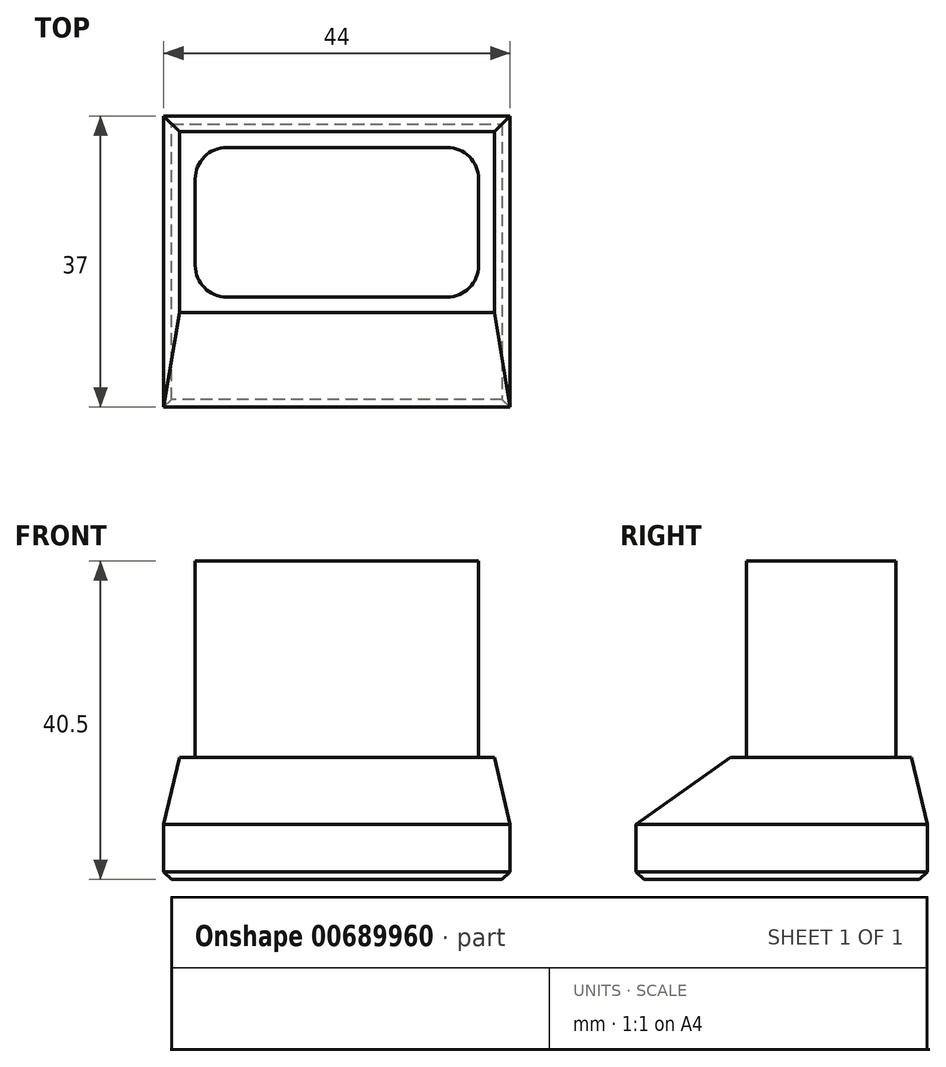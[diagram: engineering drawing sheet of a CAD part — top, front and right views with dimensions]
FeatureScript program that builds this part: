
annotation { "Feature Type Name" : "Feature", "Feature Type Description" : "" }
export const myFeature = defineFeature(function(context is Context, id is Id, definition is map)
    precondition{}
    {
        {
            var Q0;
            Q0=qCreatedBy(makeId("Top.planeOp"),FACE);
            var sketch = newSketch(context, id + "F0", { "sketchPlane" : qUnion([Q0])});
            skLineSegment(sketch, "E0.bottom", {"start": v(22, -18.5) * mm, "end": v(-22, -18.5) * mm});
            skLineSegment(sketch, "E0.top", {"start": v(22, 18.5) * mm, "end": v(-22, 18.5) * mm});
            skLineSegment(sketch, "E0.left", {"start": v(22, -18.5) * mm, "end": v(22, 18.5) * mm});
            skLineSegment(sketch, "E0.right", {"start": v(-22, -18.5) * mm, "end": v(-22, 18.5) * mm});
            skPoint(sketch, "E0.middle", {"position": v(0, 0) * mm});
            skSolve(sketch);
        }
        {
            var Q0;
            Q0=makeQuery(id+"F0.imprint","IMPRINT",FACE,{"disambiguationData":[TD([[makeQuery(id+"F0.imprint","IMPRINT",EDGE,{"derivedFrom":sQuery(id+"F0.wireOp",EDGE,"E0.bottom")}),-1.0]])]});
            extrude(context, id + "F1", {"entities" : qUnion([Q0]), "depth" : 15.5 * mm, "offsetDistance" : 25 * mm});
        }
        {
            var Q0;
            Q0=makeQuery(id+"F1.opExtrude","CAP_EDGE",EDGE,{"disambiguationData":[OSD([sQuery(id+"F0.wireOp",EDGE,"E0.bottom")])],"isStart":false});
            chamfer(context, id + "F2", {"entities" : qUnion([Q0]), "chamferType" : ChamferType.TWO_OFFSETS, "width1" : 8.5 * mm, "oppositeDirection" : false, "width2" : 12 * mm, "tangentPropagation" : true});
        }
        {
            var Q0;
            Q0=makeQuery(id+"F1.opExtrude","CAP_EDGE",EDGE,{"disambiguationData":[OSD([sQuery(id+"F0.wireOp",EDGE,"E0.right")])],"isStart":false});
            var Q1;
            Q1=makeQuery(id+"F1.opExtrude","CAP_EDGE",EDGE,{"disambiguationData":[OSD([sQuery(id+"F0.wireOp",EDGE,"E0.left")])],"isStart":false});
            var Q2;
            Q2=makeQuery(id+"F1.opExtrude","CAP_EDGE",EDGE,{"disambiguationData":[OSD([sQuery(id+"F0.wireOp",EDGE,"E0.top")])],"isStart":false});
            chamfer(context, id + "F3", {"entities" : qUnion([Q0, Q1, Q2]), "chamferType" : ChamferType.TWO_OFFSETS, "width1" : 8.5 * mm, "oppositeDirection" : false, "width2" : 2 * mm, "tangentPropagation" : true});
        }
        {
            var Q0;
            Q0=makeQuery(id+"F1.opExtrude","CAP_FACE",FACE,{"disambiguationData":[OSD([sQuery(id+"F0.wireOp",EDGE,"E0.bottom"),sQuery(id+"F0.wireOp",EDGE,"E0.top"),sQuery(id+"F0.wireOp",EDGE,"E0.left"),sQuery(id+"F0.wireOp",EDGE,"E0.right")])],"isStart":false});
            var sketch = newSketch(context, id + "F4", { "sketchPlane" : qUnion([Q0])});
            skLineSegment(sketch, "E1.bottom", {"start": v(18, 14.5) * mm, "end": v(-18, 14.5) * mm});
            skLineSegment(sketch, "E1.top", {"start": v(18, -4.5) * mm, "end": v(-18, -4.5) * mm});
            skLineSegment(sketch, "E1.left", {"start": v(18, 14.5) * mm, "end": v(18, -4.5) * mm});
            skLineSegment(sketch, "E1.right", {"start": v(-18, 14.5) * mm, "end": v(-18, -4.5) * mm});
            skPoint(sketch, "E1.middle", {"position": v(0, 0) * mm});
            skSolve(sketch);
        }
        {
            var Q0;
            Q0=makeQuery(id+"F4.imprint","IMPRINT",FACE,{"disambiguationData":[TD([[makeQuery(id+"F4.imprint","IMPRINT",EDGE,{"derivedFrom":sQuery(id+"F4.wireOp",EDGE,"E1.bottom")}),1.0]])]});
            extrude(context, id + "F5", {"entities" : qUnion([Q0]), "operationType" : NewBodyOperationType.ADD, "depth" : 25 * mm, "offsetDistance" : 25 * mm});
        }
        {
            var Q0;
            Q0=makeQuery(id+"F5.opExtrude","SWEPT_EDGE",EDGE,{"disambiguationData":[OSD([sQuery(id+"F4.wireOp",EDGE,"E1.top"),sQuery(id+"F4.wireOp",EDGE,"E1.right")])]});
            var Q1;
            Q1=makeQuery(id+"F5.opExtrude","SWEPT_EDGE",EDGE,{"disambiguationData":[OSD([sQuery(id+"F4.wireOp",EDGE,"E1.bottom"),sQuery(id+"F4.wireOp",EDGE,"E1.right")])]});
            var Q2;
            Q2=makeQuery(id+"F5.opExtrude","SWEPT_EDGE",EDGE,{"disambiguationData":[OSD([sQuery(id+"F4.wireOp",EDGE,"E1.top"),sQuery(id+"F4.wireOp",EDGE,"E1.left")])]});
            var Q3;
            Q3=makeQuery(id+"F5.opExtrude","SWEPT_EDGE",EDGE,{"disambiguationData":[OSD([sQuery(id+"F4.wireOp",EDGE,"E1.bottom"),sQuery(id+"F4.wireOp",EDGE,"E1.left")])]});
            fillet(context, id + "F6", {"entities" : qUnion([Q0, Q1, Q2, Q3]), "radius" : 4 * mm, "tangentPropagation" : true, "allowEdgeOverflow" : false});
        }
        {
            var Q0;
            Q0=makeQuery(id+"F1.opExtrude","CAP_EDGE",EDGE,{"disambiguationData":[OSD([sQuery(id+"F0.wireOp",EDGE,"E0.right")])],"isStart":true});
            var Q1;
            Q1=makeQuery(id+"F1.opExtrude","CAP_EDGE",EDGE,{"disambiguationData":[OSD([sQuery(id+"F0.wireOp",EDGE,"E0.top")])],"isStart":true});
            var Q2;
            Q2=makeQuery(id+"F1.opExtrude","CAP_EDGE",EDGE,{"disambiguationData":[OSD([sQuery(id+"F0.wireOp",EDGE,"E0.left")])],"isStart":true});
            var Q3;
            Q3=makeQuery(id+"F1.opExtrude","CAP_EDGE",EDGE,{"disambiguationData":[OSD([sQuery(id+"F0.wireOp",EDGE,"E0.bottom")])],"isStart":true});
            chamfer(context, id + "F7", {"entities" : qUnion([Q0, Q1, Q2, Q3]), "width" : 1 * mm, "tangentPropagation" : true});
        }
    });
